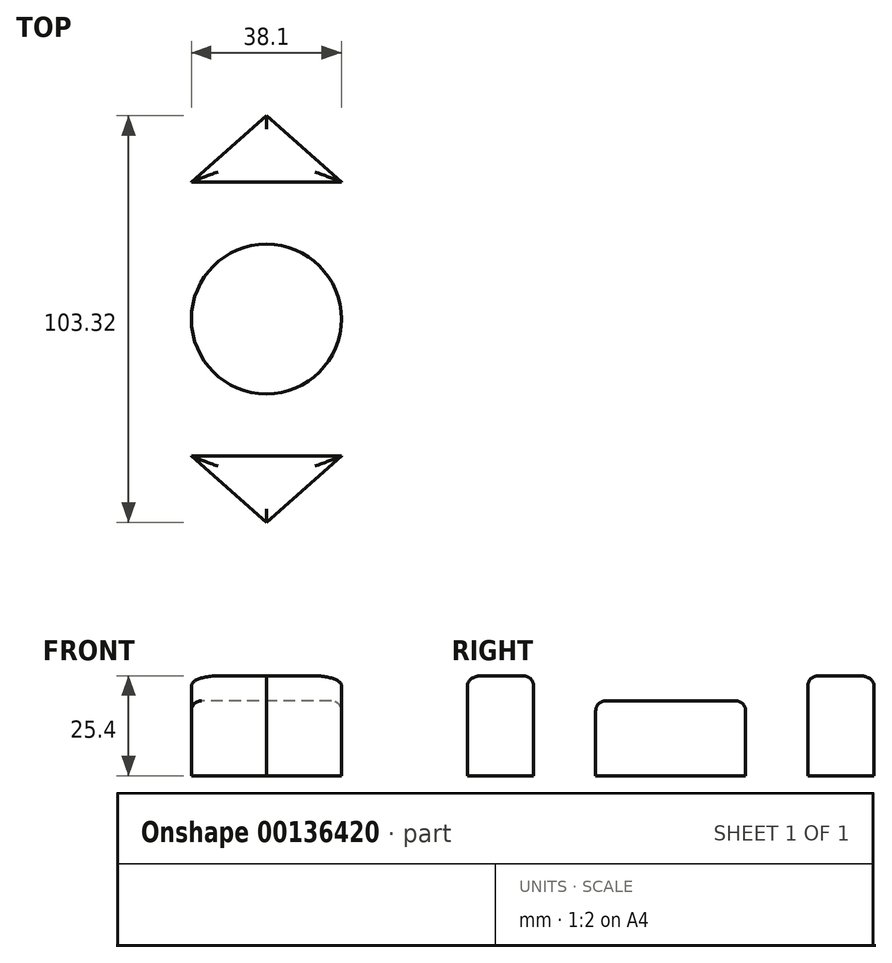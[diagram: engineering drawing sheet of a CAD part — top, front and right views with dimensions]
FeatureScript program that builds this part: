
annotation { "Feature Type Name" : "Feature", "Feature Type Description" : "" }
export const myFeature = defineFeature(function(context is Context, id is Id, definition is map)
    precondition{}
    {
        {
            var Q0;
            Q0=qCreatedBy(makeId("Top.planeOp"),FACE);
            var sketch = newSketch(context, id + "F0", { "sketchPlane" : qUnion([Q0])});
            skPoint(sketch, "E0.middle", {"position": v(0, 0) * mm});
            skLineSegment(sketch, "E1", {"start": v(-19.05, 34.86) * mm, "end": v(0, 51.66) * mm});
            skLineSegment(sketch, "E2", {"start": v(0, 51.66) * mm, "end": v(19.05, 34.86) * mm});
            skLineSegment(sketch, "E3", {"start": v(0, -34.86) * mm, "end": v(19.05, -34.86) * mm});
            skLineSegment(sketch, "E4", {"start": v(19.05, -34.86) * mm, "end": v(0, -51.66) * mm});
            skLineSegment(sketch, "E5", {"start": v(0, -51.66) * mm, "end": v(-19.05, -34.86) * mm});
            skLineSegment(sketch, "E6", {"start": v(-19.05, -34.86) * mm, "end": v(19.05, -34.86) * mm});
            skCircle(sketch, "E7", {"center": v(0, 0) * mm, "radius": 19.05 * mm});
            skLineSegment(sketch, "E8", {"start": v(-19.05, 34.86) * mm, "end": v(19.05, 34.86) * mm});
            skSolve(sketch);
        }
        {
            var Q0;
            {var subQ3=sQuery(id+"F0.wireOp",EDGE,"E2");Q0=makeQuery(id+"F0.imprint","IMPRINT",FACE,{"disambiguationData":[TD([[makeQuery(id+"F0.imprint","IMPRINT",EDGE,{"derivedFrom":subQ3}),-1.0]])]});}
            var Q1;
            {var subQ3=sQuery(id+"F0.wireOp",EDGE,"E1");Q1=makeQuery(id+"F0.imprint","IMPRINT",FACE,{"disambiguationData":[TD([[makeQuery(id+"F0.imprint","IMPRINT",EDGE,{"derivedFrom":subQ3}),-1.0]])]});}
            var Q2;
            {var subQ3=sQuery(id+"F0.wireOp",EDGE,"E4");Q2=makeQuery(id+"F0.imprint","IMPRINT",FACE,{"disambiguationData":[TD([[makeQuery(id+"F0.imprint","IMPRINT",EDGE,{"derivedFrom":subQ3}),-1.0]])]});}
            var Q3;
            {var subQ3=sQuery(id+"F0.wireOp",EDGE,"E5");Q3=makeQuery(id+"F0.imprint","IMPRINT",FACE,{"disambiguationData":[TD([[makeQuery(id+"F0.imprint","IMPRINT",EDGE,{"derivedFrom":subQ3}),-1.0]])]});}
            extrude(context, id + "F1", {"entities" : qUnion([Q0, Q1, Q2, Q3]), "depth" : 25.4 * mm});
        }
        {
            var Q0;
            Q0=makeQuery(id+"F0.imprint","IMPRINT",FACE,{"disambiguationData":[TD([[makeQuery(id+"F0.imprint","IMPRINT",EDGE,{"derivedFrom":sQuery(id+"F0.wireOp",EDGE,"E7")}),1.0]])]});
            extrude(context, id + "F2", {"entities" : qUnion([Q0]), "depth" : 19.05 * mm});
        }
        {
            var Q0;
            Q0=makeQuery(id+"F2.opExtrude","CAP_EDGE",EDGE,{"disambiguationData":[OSD([sQuery(id+"F0.wireOp",EDGE,"E7")])],"isStart":false});
            var Q1;
            Q1=makeQuery(id+"F1.opExtrude","CAP_EDGE",EDGE,{"disambiguationData":[OSD([sQuery(id+"F0.wireOp",EDGE,"E8")])],"isStart":false});
            var Q2;
            Q2=makeQuery(id+"F1.opExtrude","CAP_EDGE",EDGE,{"disambiguationData":[OSD([sQuery(id+"F0.wireOp",EDGE,"E2")])],"isStart":false});
            var Q3;
            Q3=makeQuery(id+"F1.opExtrude","CAP_EDGE",EDGE,{"disambiguationData":[OSD([sQuery(id+"F0.wireOp",EDGE,"E1")])],"isStart":false});
            var Q4;
            Q4=makeQuery(id+"F1.opExtrude","CAP_EDGE",EDGE,{"disambiguationData":[OSD([sQuery(id+"F0.wireOp",EDGE,"E5")])],"isStart":false});
            var Q5;
            Q5=makeQuery(id+"F1.opExtrude","CAP_EDGE",EDGE,{"disambiguationData":[OSD([sQuery(id+"F0.wireOp",EDGE,"E4")])],"isStart":false});
            var Q6;
            Q6=makeQuery(id+"F1.opExtrude","CAP_EDGE",EDGE,{"disambiguationData":[OSD([sQuery(id+"F0.wireOp",EDGE,"E6")])],"isStart":false});
            fillet(context, id + "F3", {"entities" : qUnion([Q0, Q1, Q2, Q3, Q4, Q5, Q6]), "radius" : 2.54 * mm, "tangentPropagation" : true, "allowEdgeOverflow" : false});
        }
    });
